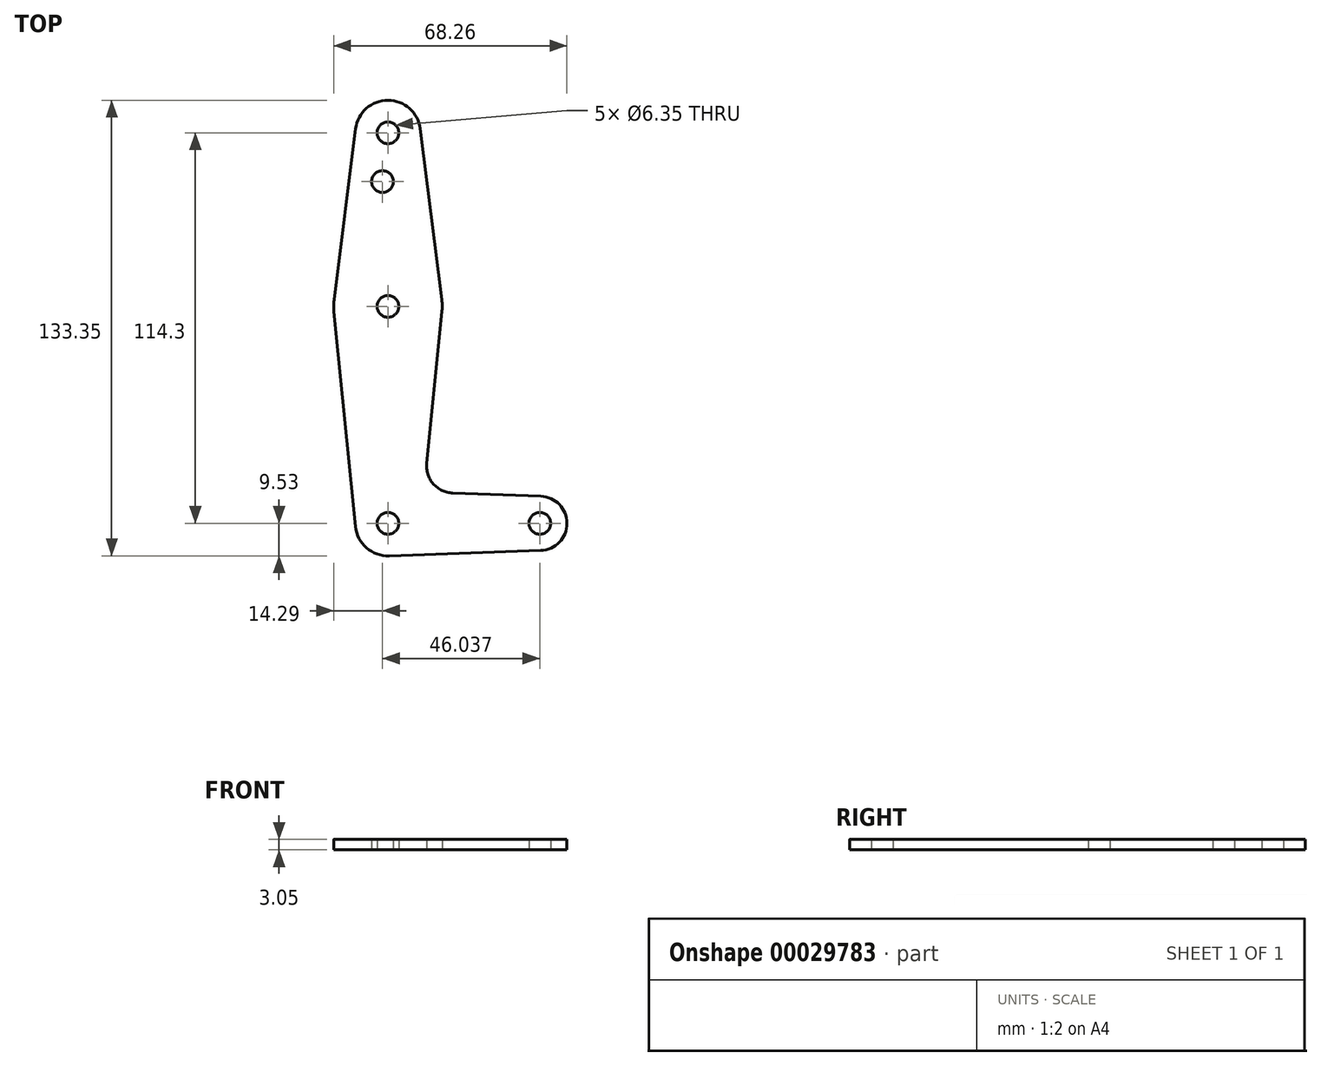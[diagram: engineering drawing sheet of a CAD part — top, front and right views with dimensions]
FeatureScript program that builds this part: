
annotation { "Feature Type Name" : "Feature", "Feature Type Description" : "" }
export const myFeature = defineFeature(function(context is Context, id is Id, definition is map)
    precondition{}
    {
        {
            var Q0;
            Q0=qCreatedBy(makeId("Top.planeOp"),FACE);
            var sketch = newSketch(context, id + "F0", { "sketchPlane" : qUnion([Q0])});
            skLineSegment(sketch, "E0", {"start": v(-23.32, 87.79) * mm, "end": v(-23.32, -26.51) * mm, "construction": true});
            skLineSegment(sketch, "E1", {"start": v(-23.32, -26.51) * mm, "end": v(21.13, -26.51) * mm, "construction": true});
            skCircle(sketch, "E2", {"center": v(21.13, -26.51) * mm, "radius": 7.94 * mm});
            skCircle(sketch, "E3", {"center": v(-23.32, -26.51) * mm, "radius": 9.52 * mm});
            skCircle(sketch, "E4", {"center": v(-23.32, 87.79) * mm, "radius": 9.52 * mm});
            skCircle(sketch, "E5", {"center": v(-23.32, 36.99) * mm, "radius": 15.88 * mm});
            skLineSegment(sketch, "E6", {"start": v(-32.77, 88.98) * mm, "end": v(-39.07, 38.97) * mm});
            skLineSegment(sketch, "E7", {"start": v(-13.87, 88.98) * mm, "end": v(-7.57, 38.97) * mm});
            skLineSegment(sketch, "E8", {"start": v(-7.53, 35.4) * mm, "end": v(-11.98, -8.92) * mm});
            skLineSegment(sketch, "E9", {"start": v(-39.12, 35.4) * mm, "end": v(-32.8, -27.46) * mm});
            skLineSegment(sketch, "E10", {"start": v(-4.36, -17.66) * mm, "end": v(21.41, -18.58) * mm});
            skCircle(sketch, "E11", {"center": v(-23.32, 87.79) * mm, "radius": 3.18 * mm});
            skCircle(sketch, "E12", {"center": v(-23.32, 36.99) * mm, "radius": 3.18 * mm});
            skCircle(sketch, "E13", {"center": v(-23.32, -26.51) * mm, "radius": 3.18 * mm});
            skCircle(sketch, "E14", {"center": v(21.13, -26.51) * mm, "radius": 3.18 * mm});
            skCircle(sketch, "E15", {"center": v(-24.91, 73.52) * mm, "radius": 3.18 * mm});
            skArc(sketch, "E16.filletArc", {"start": v(-11.98, -8.92) * mm, "mid": v(-10.06, -14.94) * mm, "end": v(-4.36, -17.66) * mm});
            skLineSegment(sketch, "E17", {"start": v(21.41, -34.44) * mm, "end": v(-22.98, -36.03) * mm});
            skSolve(sketch);
        }
        {
            var Q0;
            Q0=makeQuery(id+"F0.imprint","IMPRINT",FACE,{"disambiguationData":[TD([[makeQuery(id+"F0.imprint","IMPRINT",EDGE,{"derivedFrom":sQuery(id+"F0.wireOp",EDGE,"E14")}),-1.0]])]});
            var Q1;
            Q1=makeQuery(id+"F0.imprint","IMPRINT",FACE,{"disambiguationData":[TD([[makeQuery(id+"F0.imprint","IMPRINT",EDGE,{"derivedFrom":sQuery(id+"F0.wireOp",EDGE,"E13")}),-1.0]])]});
            var Q2;
            Q2=makeQuery(id+"F0.imprint","IMPRINT",FACE,{"disambiguationData":[TD([[makeQuery(id+"F0.imprint","IMPRINT",EDGE,{"derivedFrom":sQuery(id+"F0.wireOp",EDGE,"E11")}),-1.0]])]});
            var Q3;
            {var subQ4=sQuery(id+"F0.wireOp",EDGE,"E8");Q3=makeQuery(id+"F0.imprint","IMPRINT",FACE,{"disambiguationData":[TD([[makeQuery(id+"F0.imprint","IMPRINT",EDGE,{"derivedFrom":subQ4}),-1.0]])]});}
            var Q4;
            {var subQ1=sQuery(id+"F0.wireOp",EDGE,"E6");Q4=makeQuery(id+"F0.imprint","IMPRINT",FACE,{"disambiguationData":[TD([[makeQuery(id+"F0.imprint","IMPRINT",EDGE,{"derivedFrom":subQ1}),1.0]])]});}
            var Q5;
            Q5=makeQuery(id+"F0.imprint","IMPRINT",FACE,{"disambiguationData":[TD([[makeQuery(id+"F0.imprint","IMPRINT",EDGE,{"derivedFrom":sQuery(id+"F0.wireOp",EDGE,"E12")}),-1.0]])]});
            extrude(context, id + "F1", {"entities" : qUnion([Q0, Q1, Q2, Q3, Q4, Q5]), "depth" : 3.05 * mm});
        }
    });
